# Revit family: Sanext_Угольник-переходник с внутренней резьбой
name_source: partatom
category: Соединительные детали трубопроводов
revit_build: Autodesk Revit 2017 (Build: 20160225_1515(x64)
units: mm (PartAtom-declared; Revit-internal decimal feet)

## family parameters
Всегда вертикально = Да
На основе рабочей плоскости = Нет
Общий = Нет
При загрузке вырезать с полостями = Нет
Размер круглого соединителя = Использовать радиус
Тип детали = Отвод

## types (4) — shared parameters
ADSK_Единица измерения = шт
ADSK_Завод-изготовитель = Sanext
URL = http://sanext.ru
Изготовитель = Sanext
Материал фитинга = DZR латунь
Разработчик = ООО ПРОРУБИМ
Разработчик (телефон) = +7(495)649-85-43
Разработчик модели (URL) = http://prorubim.com
zero-valued in all types: ADSK_Масса

## per-type parameters (varying)
| type | ADSK_Код изделия | D1 | DN | G | R1 | R2 | S | a | a1 | b | c |
| Угольник-переходник с внутренней резьбой 25xG3/4 | 4941 | 30 мм | 25 мм | 25 мм | 13 мм | 13 мм | 34 мм | 61 мм | 21 мм | 29 мм | 34 мм |
| Угольник-переходник с внутренней резьбой 20xG3/4 | 4940 | 25 мм | 20 мм | 25 мм | 10 мм | 13 мм | 34 мм | 55 мм | 19 мм | 29 мм | 34 мм |
| Угольник-переходник с внутренней резьбой 20xG1/2 | 4931 | 25 мм | 20 мм | 20 мм | 10 мм | 10 мм | 25 мм | 49 мм | 17 мм | 29 мм | 25 мм |
| Угольник-переходник с внутренней резьбой 16xG1/2 | 4930 | 21 мм | 16 мм | 20 мм | 8 мм | 10 мм | 25 мм | 44 мм | 15 мм | 28 мм | 25 мм |

note: column(s) folded — value = type name in every type: ADSK_Наименование
